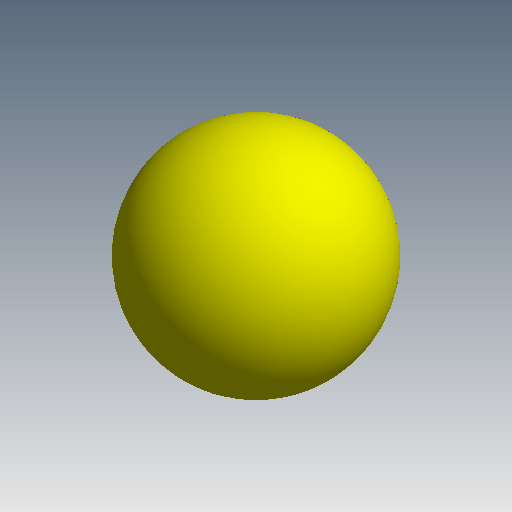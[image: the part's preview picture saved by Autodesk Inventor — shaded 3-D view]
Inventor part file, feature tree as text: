
AUTODESK INVENTOR PART (.ipt)
format: ipt  version: 2020 (Build 240168000, 168)  size: 118,784 bytes
history: native  units: mm (DEFAULTED — no unit token found)
features: revolve x1, sketch x1
ambient origin geometry x8: Origin, YZ Plane, XZ Plane, XY Plane, X Axis, Y Axis, Z Axis, Center Point
bodies: Solid1 (feature_tree)
feature tree (2):
  revolve  "Revolution1"  [1 undecoded]
  sketch  "Sketch_6"  dims[d0=360.0deg]
note: 1 required parameter value undecoded (feature->parameter linkage not recoverable at this tier; creation-order binding heuristic only, values carry confidence <= 0.55)
